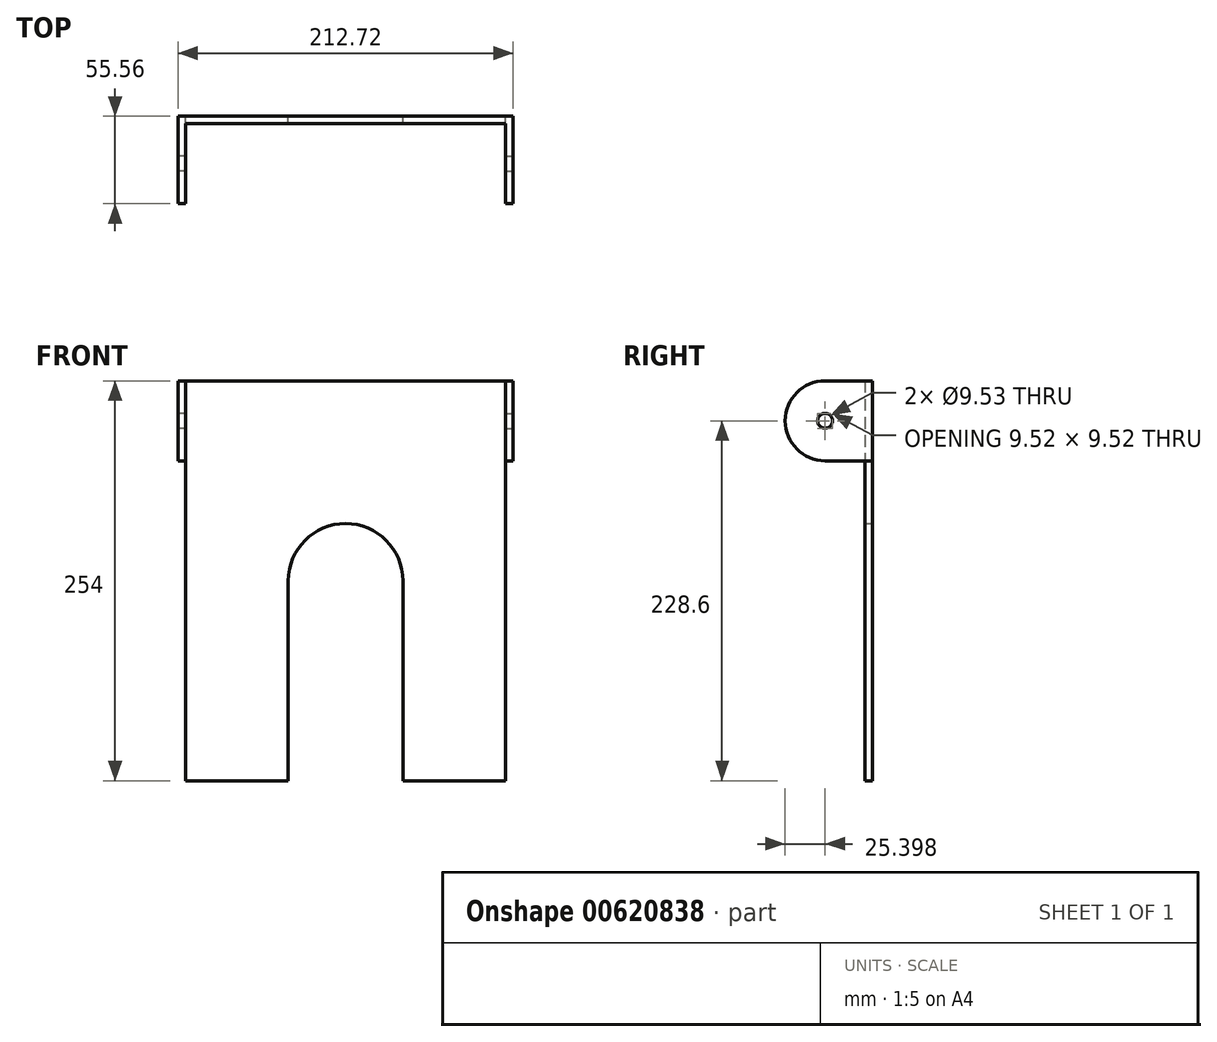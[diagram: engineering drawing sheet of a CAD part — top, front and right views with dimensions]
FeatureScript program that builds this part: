
annotation { "Feature Type Name" : "Feature", "Feature Type Description" : "" }
export const myFeature = defineFeature(function(context is Context, id is Id, definition is map)
    precondition{}
    {
        {
            var Q0;
            Q0=qCreatedBy(makeId("Front.planeOp"),FACE);
            var sketch = newSketch(context, id + "F0", { "sketchPlane" : qUnion([Q0])});
            skLineSegment(sketch, "E0.top", {"start": v(-101.6, -127) * mm, "end": v(-36.36, -127) * mm});
            skLineSegment(sketch, "E0.left", {"start": v(-101.6, 127) * mm, "end": v(-101.6, -127) * mm});
            skLineSegment(sketch, "E0.right", {"start": v(-36.36, 0) * mm, "end": v(-36.36, -127) * mm});
            skPoint(sketch, "E1", {"position": v(-36.36, 0) * mm});
            skArc(sketch, "E2", {"start": v(0, 36.36) * mm, "mid": v(-25.71, 25.71) * mm, "end": v(-36.36, 0) * mm});
            skLineSegment(sketch, "E3", {"start": v(0, 127) * mm, "end": v(0, 36.36) * mm});
            skLineSegment(sketch, "E4", {"start": v(-101.6, 127) * mm, "end": v(0, 127) * mm});
            skSolve(sketch);
        }
        {
            var Q0;
            Q0=makeQuery(id+"F0.imprint","IMPRINT",FACE,{"disambiguationData":[TD([[makeQuery(id+"F0.imprint","IMPRINT",EDGE,{"derivedFrom":sQuery(id+"F0.wireOp",EDGE,"E0.top")}),1.0]])]});
            extrude(context, id + "F1", {"entities" : qUnion([Q0]), "depth" : 4.76 * mm, "offsetDistance" : 25.4 * mm});
        }
        {
            var Q0;
            Q0=qCreatedBy(makeId("Front.planeOp"),FACE);
            var sketch = newSketch(context, id + "F2", { "sketchPlane" : qUnion([Q0])});
            skLineSegment(sketch, "E5.bottom", {"start": v(-101.6, 127) * mm, "end": v(-106.36, 127) * mm});
            skLineSegment(sketch, "E5.top", {"start": v(-101.6, 76.2) * mm, "end": v(-106.36, 76.2) * mm});
            skLineSegment(sketch, "E5.left", {"start": v(-101.6, 127) * mm, "end": v(-101.6, 76.2) * mm});
            skLineSegment(sketch, "E5.right", {"start": v(-106.36, 127) * mm, "end": v(-106.36, 76.2) * mm});
            skSolve(sketch);
        }
        {
            var Q0;
            Q0 = qSketchRegion(id + "F2", true);
            extrude(context, id + "F3", {"entities" : qUnion([Q0]), "depth" : 55.56 * mm, "offsetDistance" : 25.4 * mm});
        }
        {
            var Q0;
            Q0=makeQuery(id+"F3.opExtrude","SWEPT_FACE",FACE,{"disambiguationData":[OSD([sQuery(id+"F2.wireOp",EDGE,"E5.right")])]});
            var sketch = newSketch(context, id + "F4", { "sketchPlane" : qUnion([Q0])});
            skCircle(sketch, "E6", {"center": v(30.16, 101.6) * mm, "radius": 4.76 * mm});
            skSolve(sketch);
        }
        {
            var Q0;
            Q0 = qSketchRegion(id + "F4", true);
            var Q1;
            Q1=makeQuery(id+"F3.opExtrude","SWEPT_FACE",FACE,{"disambiguationData":[OSD([sQuery(id+"F2.wireOp",EDGE,"E5.left")])]});
            extrude(context, id + "F5", {"entities" : qUnion([Q0]), "operationType" : NewBodyOperationType.REMOVE, "endBound" : BoundingType.UP_TO_SURFACE, "oppositeDirection" : true, "depth" : 25.4 * mm, "endBoundEntityFace" : qUnion([Q1]), "offsetDistance" : 25.4 * mm});
        }
        {
            var Q0;
            Q0=makeQuery(id+"F3.opExtrude","CAP_EDGE",EDGE,{"disambiguationData":[OSD([sQuery(id+"F2.wireOp",EDGE,"E5.bottom")])],"isStart":false});
            var Q1;
            Q1=makeQuery(id+"F3.opExtrude","CAP_EDGE",EDGE,{"disambiguationData":[OSD([sQuery(id+"F2.wireOp",EDGE,"E5.top")])],"isStart":false});
            fillet(context, id + "F6", {"entities" : qUnion([Q0, Q1]), "radius" : 25.4 * mm, "tangentPropagation" : true, "allowEdgeOverflow" : false});
        }
        {
            var Q0;
            Q0=makeQuery(id+"F3.opExtrude","SWEPT_BODY",BODY,{"disambiguationData":[OSD([sQuery(id+"F2.wireOp",EDGE,"E5.bottom"),sQuery(id+"F2.wireOp",EDGE,"E5.top"),sQuery(id+"F2.wireOp",EDGE,"E5.left"),sQuery(id+"F2.wireOp",EDGE,"E5.right")])]});
            var Q1;
            Q1=makeQuery(id+"F1.opExtrude","SWEPT_BODY",BODY,{"disambiguationData":[OSD([sQuery(id+"F0.wireOp",EDGE,"E0.top"),sQuery(id+"F0.wireOp",EDGE,"E0.left"),sQuery(id+"F0.wireOp",EDGE,"E0.right"),sQuery(id+"F0.wireOp",EDGE,"E2"),sQuery(id+"F0.wireOp",EDGE,"E3"),sQuery(id+"F0.wireOp",EDGE,"E4")])]});
            var Q2;
            Q2=qCreatedBy(makeId("Right.planeOp"),FACE);
            mirror(context, id + "F7", {"operationType" : NewBodyOperationType.ADD, "entities" : qUnion([Q0, Q1]), "mirrorPlane" : qUnion([Q2])});
        }
    });
